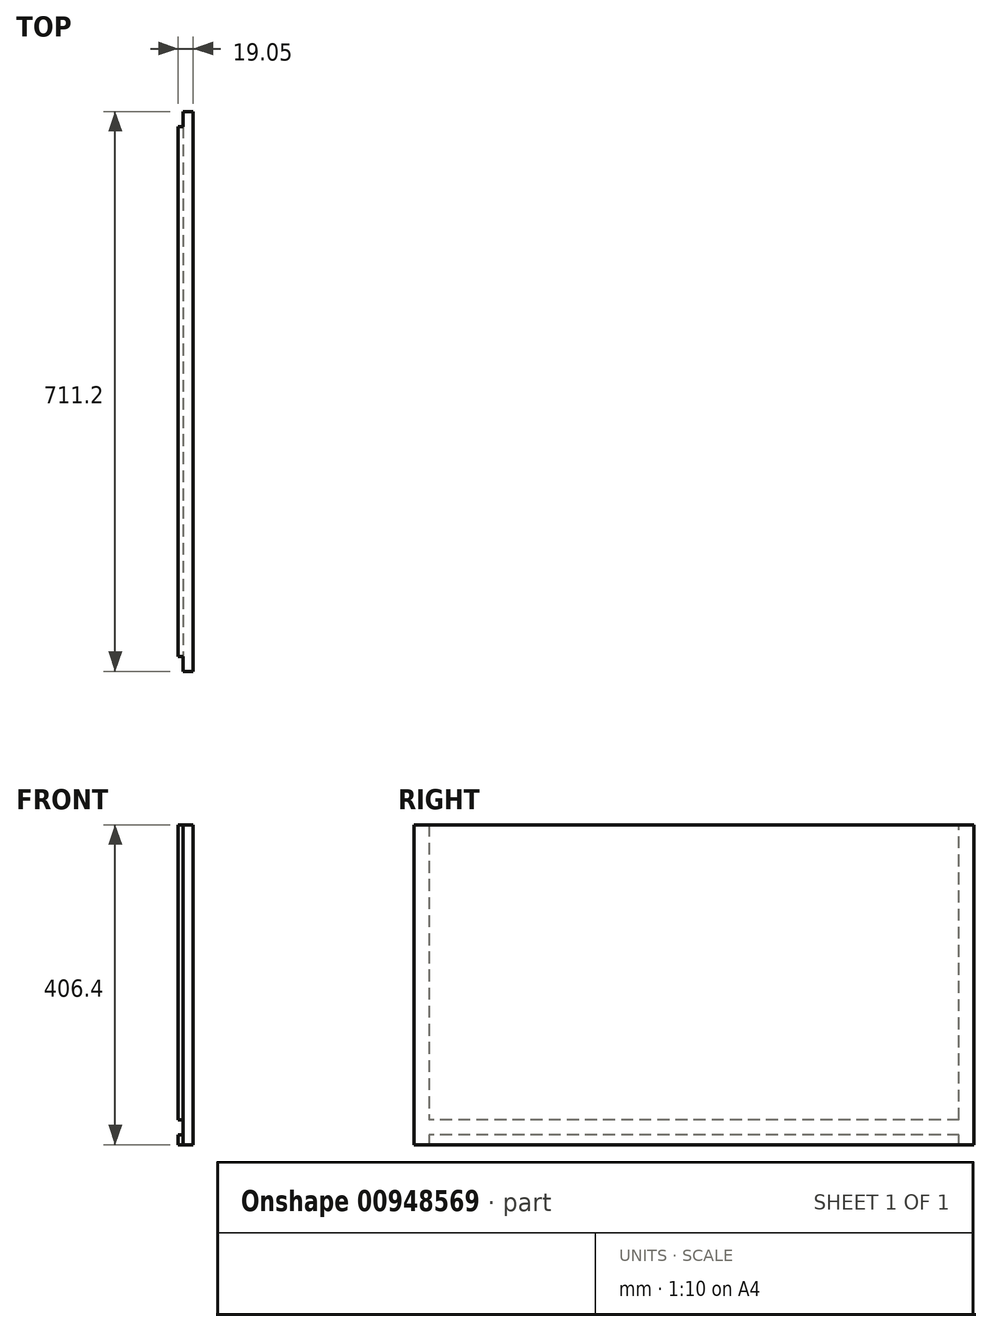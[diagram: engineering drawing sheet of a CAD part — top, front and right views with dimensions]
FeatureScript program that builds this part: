
annotation { "Feature Type Name" : "Feature", "Feature Type Description" : "" }
export const myFeature = defineFeature(function(context is Context, id is Id, definition is map)
    precondition{}
    {
        {
            var Q0;
            Q0=qCreatedBy(makeId("Right.planeOp"),FACE);
            var sketch = newSketch(context, id + "F0", { "sketchPlane" : qUnion([Q0])});
            skLineSegment(sketch, "E0.bottom", {"start": v(355.6, 203.2) * mm, "end": v(-355.6, 203.2) * mm});
            skLineSegment(sketch, "E0.top", {"start": v(355.6, -203.2) * mm, "end": v(-355.6, -203.2) * mm});
            skLineSegment(sketch, "E0.left", {"start": v(355.6, 203.2) * mm, "end": v(355.6, -203.2) * mm});
            skLineSegment(sketch, "E0.right", {"start": v(-355.6, 203.2) * mm, "end": v(-355.6, -203.2) * mm});
            skPoint(sketch, "E0.middle", {"position": v(0, 0) * mm});
            skSolve(sketch);
        }
        {
            var Q0;
            Q0=makeQuery(id+"F0.imprint","IMPRINT",FACE,{"disambiguationData":[TD([[makeQuery(id+"F0.imprint","IMPRINT",EDGE,{"derivedFrom":sQuery(id+"F0.wireOp",EDGE,"E0.bottom")}),1.0]])]});
            extrude(context, id + "F1", {"entities" : qUnion([Q0]), "depth" : 19.05 * mm, "offsetDistance" : 25.4 * mm});
        }
        {
            var Q0;
            Q0=makeQuery(id+"F1.opExtrude","CAP_FACE",FACE,{"disambiguationData":[OSD([sQuery(id+"F0.wireOp",EDGE,"E0.bottom"),sQuery(id+"F0.wireOp",EDGE,"E0.top"),sQuery(id+"F0.wireOp",EDGE,"E0.left"),sQuery(id+"F0.wireOp",EDGE,"E0.right")])],"isStart":true});
            var sketch = newSketch(context, id + "F2", { "sketchPlane" : qUnion([Q0])});
            skLineSegment(sketch, "E1.bottom", {"start": v(-355.6, -171.45) * mm, "end": v(355.6, -171.45) * mm});
            skLineSegment(sketch, "E1.top", {"start": v(-355.6, -190.5) * mm, "end": v(355.6, -190.5) * mm});
            skLineSegment(sketch, "E1.left", {"start": v(-355.6, -171.45) * mm, "end": v(-355.6, -190.5) * mm});
            skLineSegment(sketch, "E1.right", {"start": v(355.6, -171.45) * mm, "end": v(355.6, -190.5) * mm});
            skLineSegment(sketch, "E2.bottom", {"start": v(-336.55, -203.2) * mm, "end": v(-355.6, -203.2) * mm});
            skLineSegment(sketch, "E2.top", {"start": v(-336.55, 203.2) * mm, "end": v(-355.6, 203.2) * mm});
            skLineSegment(sketch, "E2.left", {"start": v(-336.55, -203.2) * mm, "end": v(-336.55, 203.2) * mm});
            skLineSegment(sketch, "E2.right", {"start": v(-355.6, -203.2) * mm, "end": v(-355.6, 203.2) * mm});
            skLineSegment(sketch, "E3.bottom", {"start": v(336.55, 203.2) * mm, "end": v(355.6, 203.2) * mm});
            skLineSegment(sketch, "E3.top", {"start": v(336.55, -203.2) * mm, "end": v(355.6, -203.2) * mm});
            skLineSegment(sketch, "E3.left", {"start": v(336.55, 203.2) * mm, "end": v(336.55, -203.2) * mm});
            skLineSegment(sketch, "E3.right", {"start": v(355.6, 203.2) * mm, "end": v(355.6, -203.2) * mm});
            skSolve(sketch);
        }
        {
            var Q0;
            Q0=makeQuery(id+"F2.imprint","IMPRINT",FACE,{"disambiguationData":[TD([[makeQuery(id+"F2.imprint","IMPRINT",EDGE,{"derivedFrom":sQuery(id+"F2.wireOp",EDGE,"E1.bottom")}),-1.0]])]});
            var Q1;
            {var subQ5=sQuery(id+"F2.wireOp",EDGE,"E2.top");Q1=makeQuery(id+"F2.imprint","IMPRINT",FACE,{"disambiguationData":[TD([[makeQuery(id+"F2.imprint","IMPRINT",EDGE,{"derivedFrom":subQ5}),-1.0]])]});}
            var Q2;
            {var subQ5=sQuery(id+"F2.wireOp",EDGE,"E2.bottom");Q2=makeQuery(id+"F2.imprint","IMPRINT",FACE,{"disambiguationData":[TD([[makeQuery(id+"F2.imprint","IMPRINT",EDGE,{"derivedFrom":subQ5}),1.0]])]});}
            var Q3;
            {var subQ5=sQuery(id+"F2.wireOp",EDGE,"E3.bottom");Q3=makeQuery(id+"F2.imprint","IMPRINT",FACE,{"disambiguationData":[TD([[makeQuery(id+"F2.imprint","IMPRINT",EDGE,{"derivedFrom":subQ5}),-1.0]])]});}
            var Q4;
            {var subQ5=sQuery(id+"F2.wireOp",EDGE,"E3.top");Q4=makeQuery(id+"F2.imprint","IMPRINT",FACE,{"disambiguationData":[TD([[makeQuery(id+"F2.imprint","IMPRINT",EDGE,{"derivedFrom":subQ5}),1.0]])]});}
            extrude(context, id + "F3", {"entities" : qUnion([Q0, Q1, Q2, Q3, Q4]), "operationType" : NewBodyOperationType.REMOVE, "oppositeDirection" : true, "depth" : 6.35 * mm, "offsetDistance" : 25.4 * mm});
        }
    });
